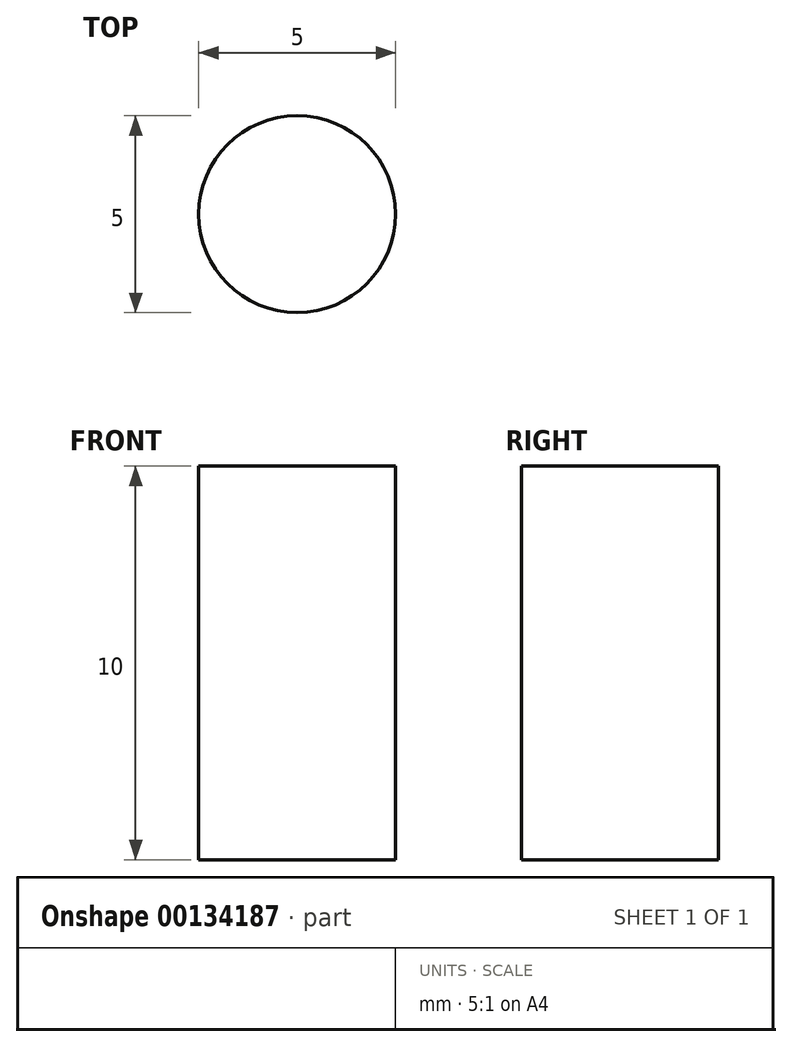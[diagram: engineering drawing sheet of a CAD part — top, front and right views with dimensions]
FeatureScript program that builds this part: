
annotation { "Feature Type Name" : "Feature", "Feature Type Description" : "" }
export const myFeature = defineFeature(function(context is Context, id is Id, definition is map)
    precondition{}
    {
        {
            var Q0;
            Q0=qCreatedBy(makeId("Top.planeOp"),FACE);
            var sketch = newSketch(context, id + "F0", { "sketchPlane" : qUnion([Q0])});
            skCircle(sketch, "E0", {"center": v(0, 0) * mm, "radius": 2.5 * mm});
            skSolve(sketch);
        }
        {
            var Q0;
            Q0=makeQuery(id+"F0.imprint","IMPRINT",FACE,{"disambiguationData":[TD([[makeQuery(id+"F0.imprint","IMPRINT",EDGE,{"derivedFrom":sQuery(id+"F0.wireOp",EDGE,"E0")}),1.0]])]});
            extrude(context, id + "F1", {"entities" : qUnion([Q0]), "depth" : 10 * mm});
        }
    });
